# Revit family: Haworth_HushMeet
name_source: partatom
category: Casework
units: mm (PartAtom-declared; Revit-internal decimal feet)

## family parameters
Always vertical = Yes
Cut with Voids When Loaded = No
OmniClass Number = 23.40.35.00
OmniClass Title = Casework
Room Calculation Point = Yes
Shared = No
Work Plane-Based = No

## types (1)
- Hush Meet
    Assembly Code = E2010200
    Back glass colour = Haworth _ Glass _ Clear
    Case = Haworth _ Laminate _ Undecided
    Construction Type = Defined construction
    Depth = 1390 mm  [stored 4.56037 ft]
    Description = Independent spaces for solo working and meetings, including virtual ones
    Door Glass = Haworth _ Glass _ Clear
    E AU = Power module : AU Type (1 x electric,1 x USB A,1 x USB C,1 x RJ45) - black
    E CH = Power module : CH (1 x electric, 2 x USB, 2 x RJ45)
    E DE = Power module : DE (1 x electric, 2 x USB, 2 x RJ45)
    E DK = Power module : DK (1 x electric, 2 x USB, 2 x RJ45)
    E GB = Power module : GB (1 x electric, 2 x USB, 2 x RJ45)
    E GB2 = Power module : GB Type (1 x electric,1 x USB A,1 x USB C,1 x RJ45) - black
    E PL/FR = Power module : PL/FR (1 x electric, 2 x USB, 2 x RJ45)
    E PL/FR2 = Power module : PL/FR Type (1 x electric,1 x USB A,1 x USB C,1 x RJ45) - black
    E US = Power module : US Type (1 x electric,1 x USB A,1 x USB C,1 x RJ45) - black
    Fabric = Haworth _ Fabric _ Undecided
    Fabric (detail) = Haworth _ Fabric _ Undecided
    Finish = Defined materials
    Frame = Haworth _ Paint _ Undecided
    Handle and hinges = Haworth _ Metal _ Undecided
    Height = 2240 mm  [stored 7.34908 ft]
    IfcExportAs = IfcFurniture
    Manufacturer = Haworth
    Middle column = Haworth _ Laminate _ Undecided
    Model = Haworth - Office Pods - HushMeet
    Revision Number = 1
    Size = Verify Final Dim. w/ Haworth
    Sustainability Info = https://www.haworth.com
    Type Image = Haworth_HushMeet.jpg
    URL = https://www.haworth.com
    URL - Product = https://www.haworth.com
    Warranty = https://cdn.shopify.com
    Width = 2150 mm  [stored 7.05381 ft]

note: [stored X ft] marks values corroborated as IEEE doubles in the binary element streams (Revit-internal decimal feet)

## geometry (parser evidence)
native form markers: Sweep x49
no freeform markers — native parametric forms only
